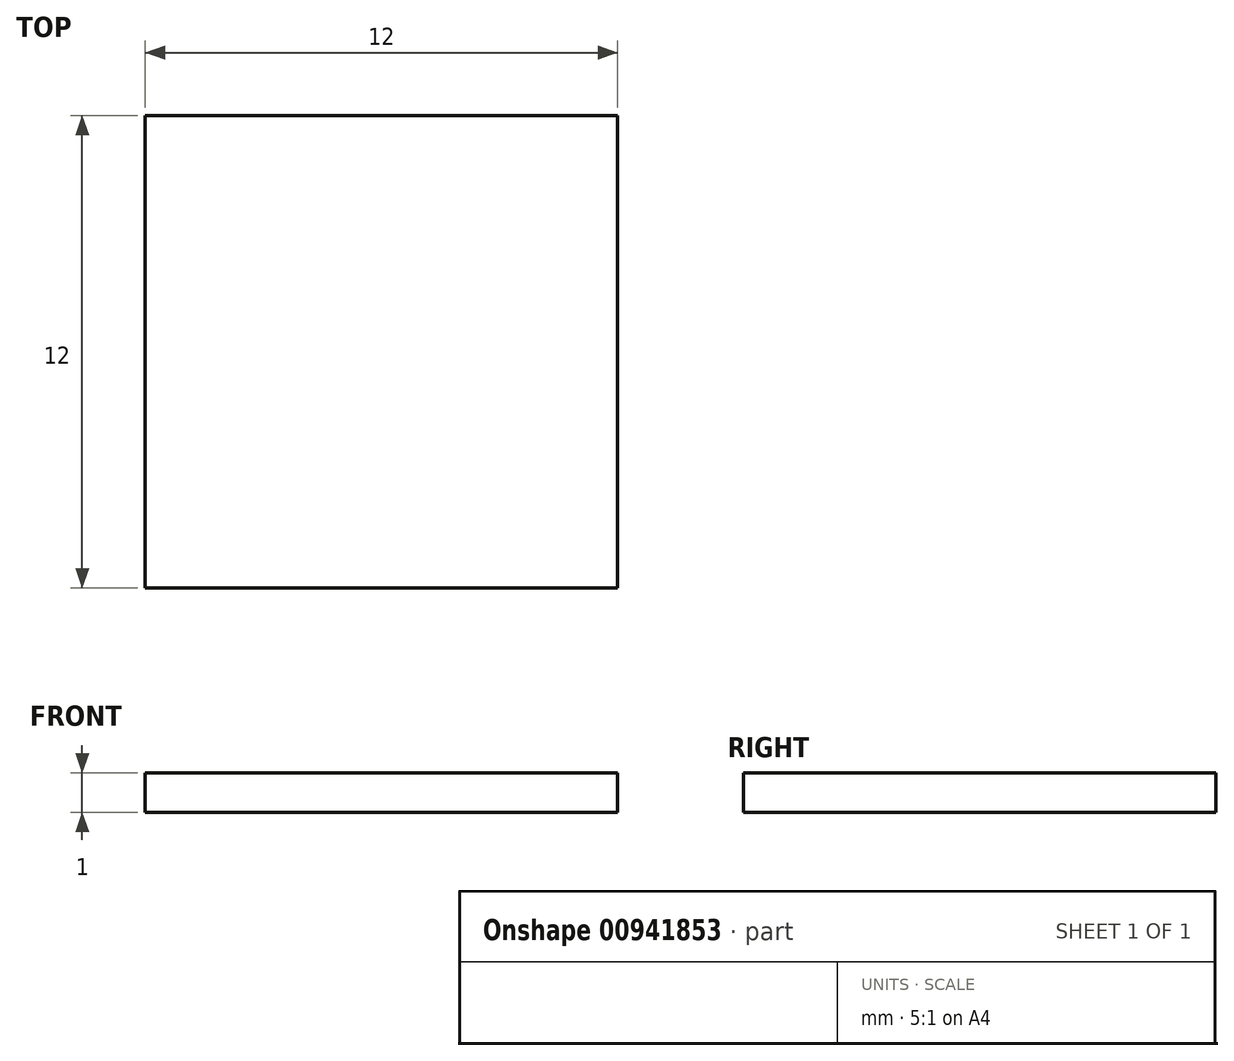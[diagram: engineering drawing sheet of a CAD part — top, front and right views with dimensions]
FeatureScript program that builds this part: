
annotation { "Feature Type Name" : "Feature", "Feature Type Description" : "" }
export const myFeature = defineFeature(function(context is Context, id is Id, definition is map)
    precondition{}
    {
        {
            var Q0;
            Q0=qCreatedBy(makeId("Top.planeOp"),FACE);
            var sketch = newSketch(context, id + "F0", { "sketchPlane" : qUnion([Q0])});
            skLineSegment(sketch, "E0.bottom", {"start": v(6, 6) * mm, "end": v(-6, 6) * mm});
            skLineSegment(sketch, "E0.top", {"start": v(6, -6) * mm, "end": v(-6, -6) * mm});
            skLineSegment(sketch, "E0.left", {"start": v(6, 6) * mm, "end": v(6, -6) * mm});
            skLineSegment(sketch, "E0.right", {"start": v(-6, 6) * mm, "end": v(-6, -6) * mm});
            skPoint(sketch, "E0.middle", {"position": v(0, 0) * mm});
            skSolve(sketch);
        }
        {
            var Q0;
            Q0=makeQuery(id+"F0.imprint","IMPRINT",FACE,{"disambiguationData":[TD([[makeQuery(id+"F0.imprint","IMPRINT",EDGE,{"derivedFrom":sQuery(id+"F0.wireOp",EDGE,"E0.bottom")}),1.0]])]});
            extrude(context, id + "F1", {"entities" : qUnion([Q0]), "depth" : 1 * mm, "offsetDistance" : 25.4 * mm});
        }
    });
